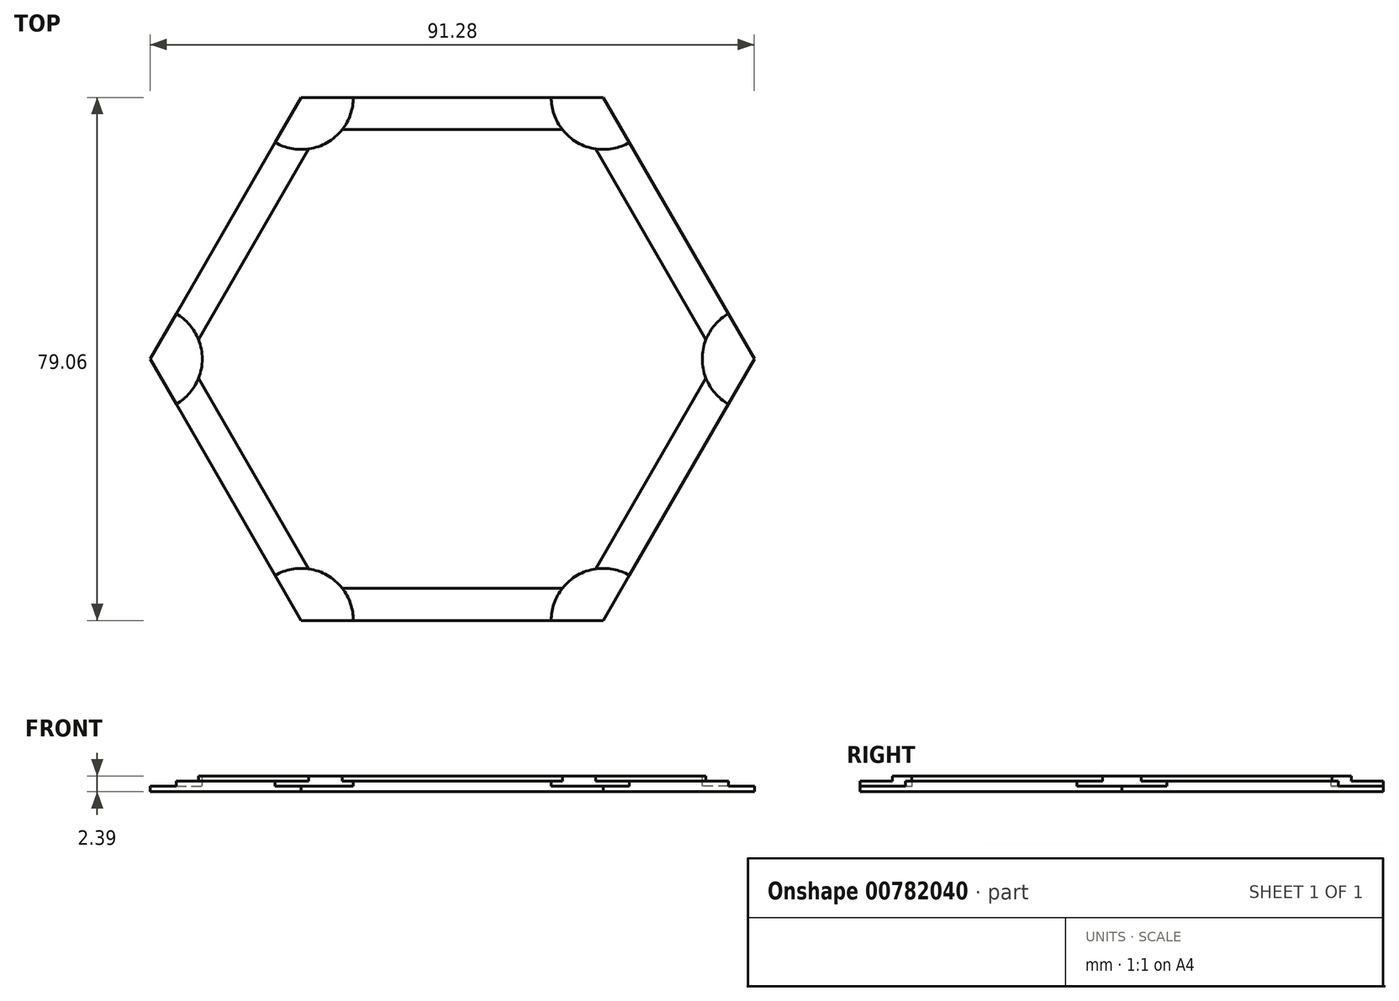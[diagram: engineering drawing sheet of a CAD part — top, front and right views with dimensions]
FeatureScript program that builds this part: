
annotation { "Feature Type Name" : "Feature", "Feature Type Description" : "" }
export const myFeature = defineFeature(function(context is Context, id is Id, definition is map)
    precondition{}
    {
        {
            var Q0;
            Q0=qCreatedBy(makeId("Top.planeOp"),FACE);
            var sketch = newSketch(context, id + "F0", { "sketchPlane" : qUnion([Q0])});
            skLineSegment(sketch, "E0", {"start": v(22.82, -39.53) * mm, "end": v(-22.82, -39.53) * mm});
            skLineSegment(sketch, "E1", {"start": v(-22.82, -39.53) * mm, "end": v(-45.64, 0) * mm});
            skLineSegment(sketch, "E2", {"start": v(-45.64, 0) * mm, "end": v(-22.82, 39.53) * mm});
            skLineSegment(sketch, "E3", {"start": v(-22.82, 39.53) * mm, "end": v(22.82, 39.53) * mm});
            skLineSegment(sketch, "E4", {"start": v(45.64, 0) * mm, "end": v(22.82, -39.53) * mm});
            skLineSegment(sketch, "E5", {"start": v(22.82, 39.53) * mm, "end": v(45.64, 0) * mm});
            skLineSegment(sketch, "E6", {"start": v(-22.82, -39.53) * mm, "end": v(22.82, 39.53) * mm, "construction": true});
            skSolve(sketch);
        }
        {
            var Q0;
            Q0 = qSketchRegion(id + "F0", true);
            extrude(context, id + "F1", {"entities" : qUnion([Q0]), "depth" : 1.63 * mm, "offsetDistance" : 25.4 * mm});
        }
        {
            var Q0;
            Q0=qCreatedBy(makeId("Top.planeOp"),FACE);
            var sketch = newSketch(context, id + "F2", { "sketchPlane" : qUnion([Q0])});
            skLineSegment(sketch, "E7.0", {"start": v(20, -34.65) * mm, "end": v(40.01, 0) * mm});
            skLineSegment(sketch, "E7.1", {"start": v(20, 34.65) * mm, "end": v(-20, 34.65) * mm});
            skLineSegment(sketch, "E7.2", {"start": v(-20, 34.65) * mm, "end": v(-40.01, 0) * mm});
            skLineSegment(sketch, "E7.3", {"start": v(40.01, 0) * mm, "end": v(20, 34.65) * mm});
            skLineSegment(sketch, "E7.4", {"start": v(-40.01, 0) * mm, "end": v(-20, -34.65) * mm});
            skLineSegment(sketch, "E7.5", {"start": v(-20, -34.65) * mm, "end": v(20, -34.65) * mm});
            skLineSegment(sketch, "E8.0", {"start": v(19.16, -33.18) * mm, "end": v(38.31, 0) * mm});
            skLineSegment(sketch, "E8.1", {"start": v(19.16, 33.18) * mm, "end": v(-19.16, 33.18) * mm});
            skLineSegment(sketch, "E8.2", {"start": v(-19.16, 33.18) * mm, "end": v(-38.31, 0) * mm});
            skLineSegment(sketch, "E8.4", {"start": v(-38.31, 0) * mm, "end": v(-19.16, -33.18) * mm});
            skLineSegment(sketch, "E8.5", {"start": v(-19.16, -33.18) * mm, "end": v(19.16, -33.18) * mm});
            skSolve(sketch);
        }
        {
            var Q0;
            Q0 = qSketchRegion(id + "F2", true);
            extrude(context, id + "F3", {"entities" : qUnion([Q0]), "operationType" : NewBodyOperationType.ADD, "depth" : 2.4 * mm, "offsetDistance" : 25.4 * mm});
        }
        {
            var Q0;
            Q0=makeQuery(id+"F3.opExtrude","CAP_FACE",FACE,{"disambiguationData":[OSD([sQuery(id+"F2.wireOp",EDGE,"E7.0"),sQuery(id+"F2.wireOp",EDGE,"E7.1"),sQuery(id+"F2.wireOp",EDGE,"E7.2"),sQuery(id+"F2.wireOp",EDGE,"E7.3"),sQuery(id+"F2.wireOp",EDGE,"E7.4"),sQuery(id+"F2.wireOp",EDGE,"E7.5")])],"isStart":false});
            var sketch = newSketch(context, id + "F4", { "sketchPlane" : qUnion([Q0])});
            skSolve(sketch);
        }
        {
            var Q0;
            Q0=makeQuery(id+"F4.imprint","IMPRINT",FACE,{"disambiguationData":[TD([[makeQuery(id+"F4.imprint","IMPRINT",EDGE,{"derivedFrom":makeQuery(id+"F3.opExtrude","CAP_EDGE",EDGE,{"disambiguationData":[OSD([sQuery(id+"F2.wireOp",EDGE,"E7.0")])],"isStart":false})}),1.0]])]});
            var sketch = newSketch(context, id + "F5", { "sketchPlane" : qUnion([Q0])});
            skCircle(sketch, "E9", {"center": v(22.82, -39.53) * mm, "radius": 7.87 * mm});
            skCircle(sketch, "E10", {"center": v(45.64, 0) * mm, "radius": 7.87 * mm});
            skCircle(sketch, "E11", {"center": v(22.82, 39.53) * mm, "radius": 7.87 * mm});
            skCircle(sketch, "E12", {"center": v(-22.82, 39.53) * mm, "radius": 7.87 * mm});
            skCircle(sketch, "E13", {"center": v(-45.64, 0) * mm, "radius": 7.87 * mm});
            skCircle(sketch, "E14", {"center": v(-22.82, -39.53) * mm, "radius": 7.87 * mm});
            skSolve(sketch);
        }
        {
            var Q0;
            Q0 = qSketchRegion(id + "F5", true);
            extrude(context, id + "F6", {"entities" : qUnion([Q0]), "operationType" : NewBodyOperationType.REMOVE, "oppositeDirection" : true, "depth" : 1.52 * mm, "offsetDistance" : 25.4 * mm});
        }
    });
